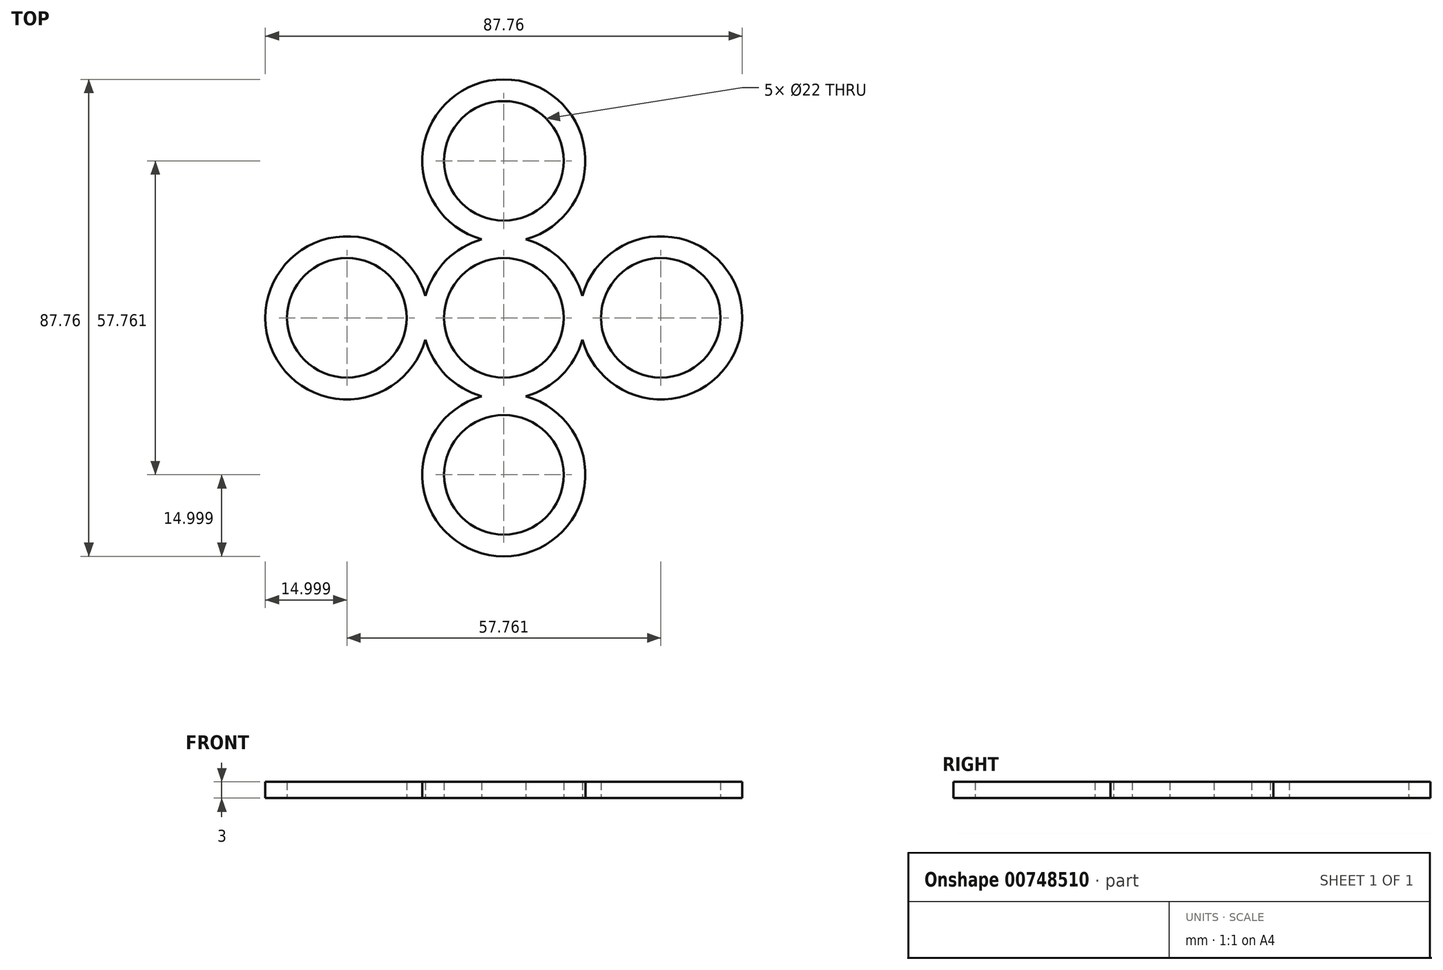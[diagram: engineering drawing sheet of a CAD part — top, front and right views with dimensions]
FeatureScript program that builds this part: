
annotation { "Feature Type Name" : "Feature", "Feature Type Description" : "" }
export const myFeature = defineFeature(function(context is Context, id is Id, definition is map)
    precondition{}
    {
        {
            var Q0;
            Q0=qCreatedBy(makeId("Top.planeOp"),FACE);
            var sketch = newSketch(context, id + "F0", { "sketchPlane" : qUnion([Q0])});
            skArc(sketch, "E0", {"start": v(7.78, 7.78) * mm, "mid": v(0, 11) * mm, "end": v(-7.78, 7.78) * mm});
            skArc(sketch, "E1", {"start": v(-4.06, 14.44) * mm, "mid": v(-7.58, 12.94) * mm, "end": v(-10.6, 10.6) * mm});
            skCircle(sketch, "E2", {"center": v(0, 28.88) * mm, "radius": 11 * mm});
            skArc(sketch, "E3", {"start": v(4.06, 14.44) * mm, "mid": v(0, 43.88) * mm, "end": v(-4.06, 14.44) * mm});
            skArc(sketch, "E4.trimOffspring", {"start": v(10.6, 10.6) * mm, "mid": v(7.58, 12.94) * mm, "end": v(4.06, 14.44) * mm});
            skCircle(sketch, "E5.1.0", {"center": v(-28.88, 0) * mm, "radius": 11 * mm});
            skArc(sketch, "E5.1.1", {"start": v(-14.44, 4.06) * mm, "mid": v(-43.88, 0) * mm, "end": v(-14.44, -4.06) * mm});
            skArc(sketch, "E5.1.2", {"start": v(-14.44, -4.06) * mm, "mid": v(-12.94, -7.58) * mm, "end": v(-10.6, -10.6) * mm});
            skArc(sketch, "E5.1.3", {"start": v(-10.6, 10.6) * mm, "mid": v(-12.94, 7.58) * mm, "end": v(-14.44, 4.06) * mm});
            skArc(sketch, "E5.1.4", {"start": v(-7.78, 7.78) * mm, "mid": v(-11, 0) * mm, "end": v(-7.78, -7.78) * mm});
            skCircle(sketch, "E5.2.0", {"center": v(0, -28.88) * mm, "radius": 11 * mm});
            skArc(sketch, "E5.2.1", {"start": v(-4.06, -14.44) * mm, "mid": v(0, -43.88) * mm, "end": v(4.06, -14.44) * mm});
            skArc(sketch, "E5.2.2", {"start": v(4.06, -14.44) * mm, "mid": v(7.58, -12.94) * mm, "end": v(10.6, -10.6) * mm});
            skArc(sketch, "E5.2.3", {"start": v(-10.6, -10.6) * mm, "mid": v(-7.58, -12.94) * mm, "end": v(-4.06, -14.44) * mm});
            skArc(sketch, "E5.2.4", {"start": v(-7.78, -7.78) * mm, "mid": v(0, -11) * mm, "end": v(7.78, -7.78) * mm});
            skCircle(sketch, "E5.3.0", {"center": v(28.88, 0) * mm, "radius": 11 * mm});
            skArc(sketch, "E5.3.1", {"start": v(14.44, -4.06) * mm, "mid": v(43.88, 0) * mm, "end": v(14.44, 4.06) * mm});
            skArc(sketch, "E5.3.2", {"start": v(14.44, 4.06) * mm, "mid": v(12.94, 7.58) * mm, "end": v(10.6, 10.6) * mm});
            skArc(sketch, "E5.3.3", {"start": v(10.6, -10.6) * mm, "mid": v(12.94, -7.58) * mm, "end": v(14.44, -4.06) * mm});
            skArc(sketch, "E5.3.4", {"start": v(7.78, -7.78) * mm, "mid": v(11, 0) * mm, "end": v(7.78, 7.78) * mm});
            skSolve(sketch);
        }
        {
            var Q0;
            Q0 = qSketchRegion(id + "F0", true);
            extrude(context, id + "F1", {"entities" : qUnion([Q0]), "depth" : 3 * mm, "offsetDistance" : 25 * mm});
        }
    });
